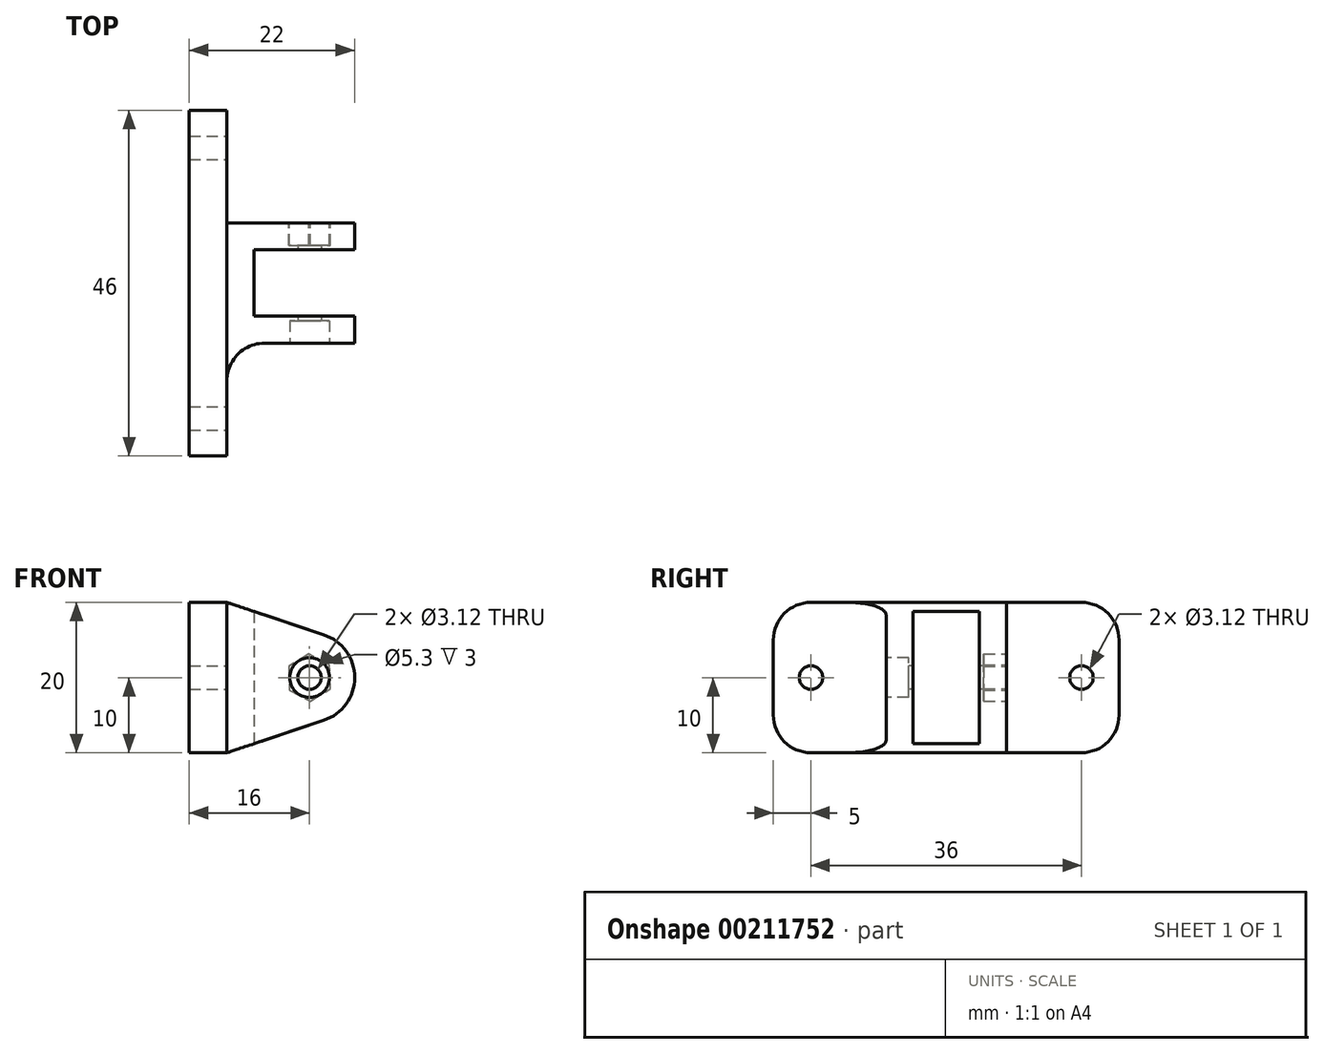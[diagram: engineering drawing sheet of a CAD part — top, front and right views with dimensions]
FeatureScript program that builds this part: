
annotation { "Feature Type Name" : "Feature", "Feature Type Description" : "" }
export const myFeature = defineFeature(function(context is Context, id is Id, definition is map)
    precondition{}
    {
        {
            var Q0;
            Q0=qCreatedBy(makeId("Front.planeOp"),FACE);
            var sketch = newSketch(context, id + "F0", { "sketchPlane" : qUnion([Q0])});
            skCircle(sketch, "E0", {"center": v(0, 0) * mm, "radius": 6 * mm});
            skLineSegment(sketch, "E1", {"start": v(-11, 10) * mm, "end": v(-11, -10) * mm});
            skLineSegment(sketch, "E2", {"start": v(-11, 10) * mm, "end": v(1.9, 5.7) * mm});
            skLineSegment(sketch, "E3", {"start": v(-11, -10) * mm, "end": v(1.9, -5.7) * mm});
            skLineSegment(sketch, "E4", {"start": v(-11, 10) * mm, "end": v(-16, 10) * mm});
            skLineSegment(sketch, "E5", {"start": v(-16, 10) * mm, "end": v(-16, -10) * mm});
            skLineSegment(sketch, "E6", {"start": v(-16, -10) * mm, "end": v(-11, -10) * mm});
            skSolve(sketch);
        }
        {
            var Q0;
            Q0=makeQuery(id+"F0.imprint","IMPRINT",FACE,{"disambiguationData":[TD([[makeQuery(id+"F0.imprint","IMPRINT",EDGE,{"derivedFrom":sQuery(id+"F0.wireOp",EDGE,"E1")}),1.0]])]});
            var Q1;
            Q1=makeQuery(id+"F0.imprint","IMPRINT",FACE,{"disambiguationData":[TD([[makeQuery(id+"F0.imprint","IMPRINT",EDGE,{"derivedFrom":sQuery(id+"F0.wireOp",EDGE,"delYWeIz-kN3U-NhPT-jKTh-7UcYjuc5mxhz")}),-1.0]])]});
            var Q2;
            {var subQ0=sQuery(id+"F0.wireOp",EDGE,"E0");var subQ1=makeQuery(id+"F0.imprint","INTERSECT",VERTEX,{"derivedFrom":[subQ0,sQuery(id+"F0.wireOp",EDGE,"E2")]});Q2=makeQuery(id+"F0.imprint","IMPRINT",FACE,{"disambiguationData":[TD([[makeQuery(id+"F0.imprint","IMPRINT",EDGE,{"disambiguationData":[TD([[subQ1,-1.0]])],"derivedFrom":subQ0}),1.0]])]});}
            extrude(context, id + "F1", {"entities" : qUnion([Q0, Q1, Q2]), "endBound" : BoundingType.SYMMETRIC, "depth" : 16 * mm});
        }
        {
            var Q0;
            Q0=makeQuery(id+"F1.opExtrude","SWEPT_FACE",FACE,{"disambiguationData":[OSD([sQuery(id+"F0.wireOp",EDGE,"E2")])]});
            var Q1;
            Q1=makeQuery(id+"F1.opExtrude","SWEPT_FACE",FACE,{"disambiguationData":[OSD([sQuery(id+"F0.wireOp",EDGE,"E0")])]});
            var Q2;
            Q2=makeQuery(id+"F1.opExtrude","SWEPT_FACE",FACE,{"disambiguationData":[OSD([sQuery(id+"F0.wireOp",EDGE,"E3")])]});
            shell(context, id + "F2", {"entities" : qUnion([Q0, Q1, Q2]), "thickness" : 3.6 * mm});
        }
        {
            var Q0;
            Q0=makeQuery(id+"F1.opExtrude","CAP_FACE",FACE,{"disambiguationData":[OSD([sQuery(id+"F0.wireOp",EDGE,"E0"),sQuery(id+"F0.wireOp",EDGE,"E1"),sQuery(id+"F0.wireOp",EDGE,"E2"),sQuery(id+"F0.wireOp",EDGE,"E3")])],"isStart":false});
            var sketch = newSketch(context, id + "F3", { "sketchPlane" : qUnion([Q0])});
            skPoint(sketch, "E7", {"position": v(0, 0) * mm});
            skSolve(sketch);
        }
        {
            var Q0;
            Q0=sQuery(id+"F3.wireOp",VERTEX,"E7");
            var Q1;
            Q1=makeQuery(id+"F1.opExtrude","SWEPT_BODY",BODY,{"disambiguationData":[OSD([sQuery(id+"F0.wireOp",EDGE,"E0"),sQuery(id+"F0.wireOp",EDGE,"E1"),sQuery(id+"F0.wireOp",EDGE,"E2"),sQuery(id+"F0.wireOp",EDGE,"E3")])]});
            hole(context, id + "F4", {"style" : HoleStyle.C_BORE, "endStyle" : HoleEndStyle.BLIND, "holeDiameter" : 3.12 * mm, "cBoreDiameter" : 5.3 * mm, "cBoreDepth" : 3 * mm, "holeDepth" : 18 * mm, "isTappedThrough" : true, "tappedDepth" : 12 * mm, "tapClearance" : 3, "startFromSketch" : true, "locations" : qUnion([Q0]), "scope" : qUnion([Q1])});
        }
        {
            var Q0;
            Q0=makeQuery(id+"F0.imprint","IMPRINT",FACE,{"disambiguationData":[TD([[makeQuery(id+"F0.imprint","IMPRINT",EDGE,{"derivedFrom":sQuery(id+"F0.wireOp",EDGE,"E1")}),-1.0]])]});
            extrude(context, id + "F5", {"entities" : qUnion([Q0]), "operationType" : NewBodyOperationType.ADD, "endBound" : BoundingType.SYMMETRIC, "depth" : 46 * mm});
        }
        {
            var Q0;
            Q0=makeQuery(id+"F1.opExtrude","CAP_FACE",FACE,{"disambiguationData":[OSD([sQuery(id+"F0.wireOp",EDGE,"E0"),sQuery(id+"F0.wireOp",EDGE,"E1"),sQuery(id+"F0.wireOp",EDGE,"E2"),sQuery(id+"F0.wireOp",EDGE,"E3")])],"isStart":true});
            var sketch = newSketch(context, id + "F6", { "sketchPlane" : qUnion([Q0])});
            skCircle(sketch, "E8.cCircle", {"center": v(0, 0) * mm, "radius": 2.73 * mm, "construction": true});
            skLineSegment(sketch, "E8.0", {"start": v(-0.12, -3.14) * mm, "end": v(-2.78, -1.47) * mm});
            skLineSegment(sketch, "E8.1", {"start": v(-2.78, -1.47) * mm, "end": v(-2.66, 1.67) * mm});
            skLineSegment(sketch, "E8.2", {"start": v(-2.66, 1.67) * mm, "end": v(0.12, 3.14) * mm});
            skLineSegment(sketch, "E8.3", {"start": v(0.12, 3.14) * mm, "end": v(2.78, 1.47) * mm});
            skLineSegment(sketch, "E8.4", {"start": v(2.78, 1.47) * mm, "end": v(2.66, -1.67) * mm});
            skLineSegment(sketch, "E8.5", {"start": v(2.66, -1.67) * mm, "end": v(-0.12, -3.14) * mm});
            skPoint(sketch, "E8.0.midPoint", {"position": v(-1.45, -2.3) * mm});
            skSolve(sketch);
        }
        {
            var Q0;
            Q0=makeQuery(id+"F6.imprint","IMPRINT",FACE,{"disambiguationData":[TD([[makeQuery(id+"F6.imprint","IMPRINT",EDGE,{"derivedFrom":sQuery(id+"F6.wireOp",EDGE,"E8.0")}),-1.0]])]});
            extrude(context, id + "F7", {"entities" : qUnion([Q0]), "operationType" : NewBodyOperationType.REMOVE, "oppositeDirection" : true, "depth" : 3 * mm});
        }
        {
            var Q0;
            {var subQ2=sQuery(id+"F0.wireOp",EDGE,"E1");var subQ3=sQuery(id+"F0.wireOp",EDGE,"E2");var subQ4=sQuery(id+"F0.wireOp",EDGE,"E3");Q0=makeQuery(id+"F5.boolean.opBoolean","SPLIT",FACE,{"disambiguationData":[TD([makeQuery(id+"F1.opExtrude","CAP_FACE",FACE,{"disambiguationData":[OSD([sQuery(id+"F0.wireOp",EDGE,"E0"),subQ2,subQ3,subQ4])],"isStart":true})])],"derivedFrom":makeQuery(id+"F5.opExtrude","SWEPT_FACE",FACE,{"disambiguationData":[OSD([subQ2])]})});}
            var sketch = newSketch(context, id + "F8", { "sketchPlane" : qUnion([Q0])});
            skPoint(sketch, "E9", {"position": v(18, 0) * mm});
            skPoint(sketch, "E9.positionSnap0", {"position": v(23, 0) * mm});
            skPoint(sketch, "E10", {"position": v(-18, 0) * mm});
            skSolve(sketch);
        }
        {
            var Q0;
            Q0=sQuery(id+"F8.wireOp",VERTEX,"E9");
            var Q1;
            Q1=sQuery(id+"F8.wireOp",VERTEX,"E10");
            var Q2;
            Q2=makeQuery(id+"F1.opExtrude","SWEPT_BODY",BODY,{"disambiguationData":[OSD([sQuery(id+"F0.wireOp",EDGE,"E0"),sQuery(id+"F0.wireOp",EDGE,"E1"),sQuery(id+"F0.wireOp",EDGE,"E2"),sQuery(id+"F0.wireOp",EDGE,"E3")])]});
            hole(context, id + "F9", {"style" : HoleStyle.SIMPLE, "endStyle" : HoleEndStyle.BLIND, "holeDiameter" : 3.12 * mm, "holeDepth" : 18 * mm, "isTappedThrough" : true, "tappedDepth" : 12 * mm, "tapClearance" : 3, "startFromSketch" : true, "locations" : qUnion([Q0, Q1]), "scope" : qUnion([Q2])});
        }
        {
            var Q0;
            Q0=makeQuery(id+"F1.opExtrude","CAP_EDGE",EDGE,{"disambiguationData":[OSD([sQuery(id+"F0.wireOp",EDGE,"E1")])],"isStart":true});
            var Q1;
            Q1=makeQuery(id+"F1.opExtrude","CAP_EDGE",EDGE,{"disambiguationData":[OSD([sQuery(id+"F0.wireOp",EDGE,"E1")])],"isStart":false});
            var Q2;
            Q2=makeQuery(id+"F5.opExtrude","CAP_EDGE",EDGE,{"disambiguationData":[OSD([sQuery(id+"F0.wireOp",EDGE,"E4")])],"isStart":true});
            var Q3;
            Q3=makeQuery(id+"F5.opExtrude","CAP_EDGE",EDGE,{"disambiguationData":[OSD([sQuery(id+"F0.wireOp",EDGE,"E6")])],"isStart":true});
            var Q4;
            Q4=makeQuery(id+"F5.opExtrude","CAP_EDGE",EDGE,{"disambiguationData":[OSD([sQuery(id+"F0.wireOp",EDGE,"E6")])],"isStart":false});
            var Q5;
            Q5=makeQuery(id+"F5.opExtrude","CAP_EDGE",EDGE,{"disambiguationData":[OSD([sQuery(id+"F0.wireOp",EDGE,"E4")])],"isStart":false});
            fillet(context, id + "F10", {"entities" : qUnion([Q0, Q1, Q2, Q3, Q4, Q5]), "radius" : 5 * mm, "tangentPropagation" : true, "allowEdgeOverflow" : false});
        }
    });
